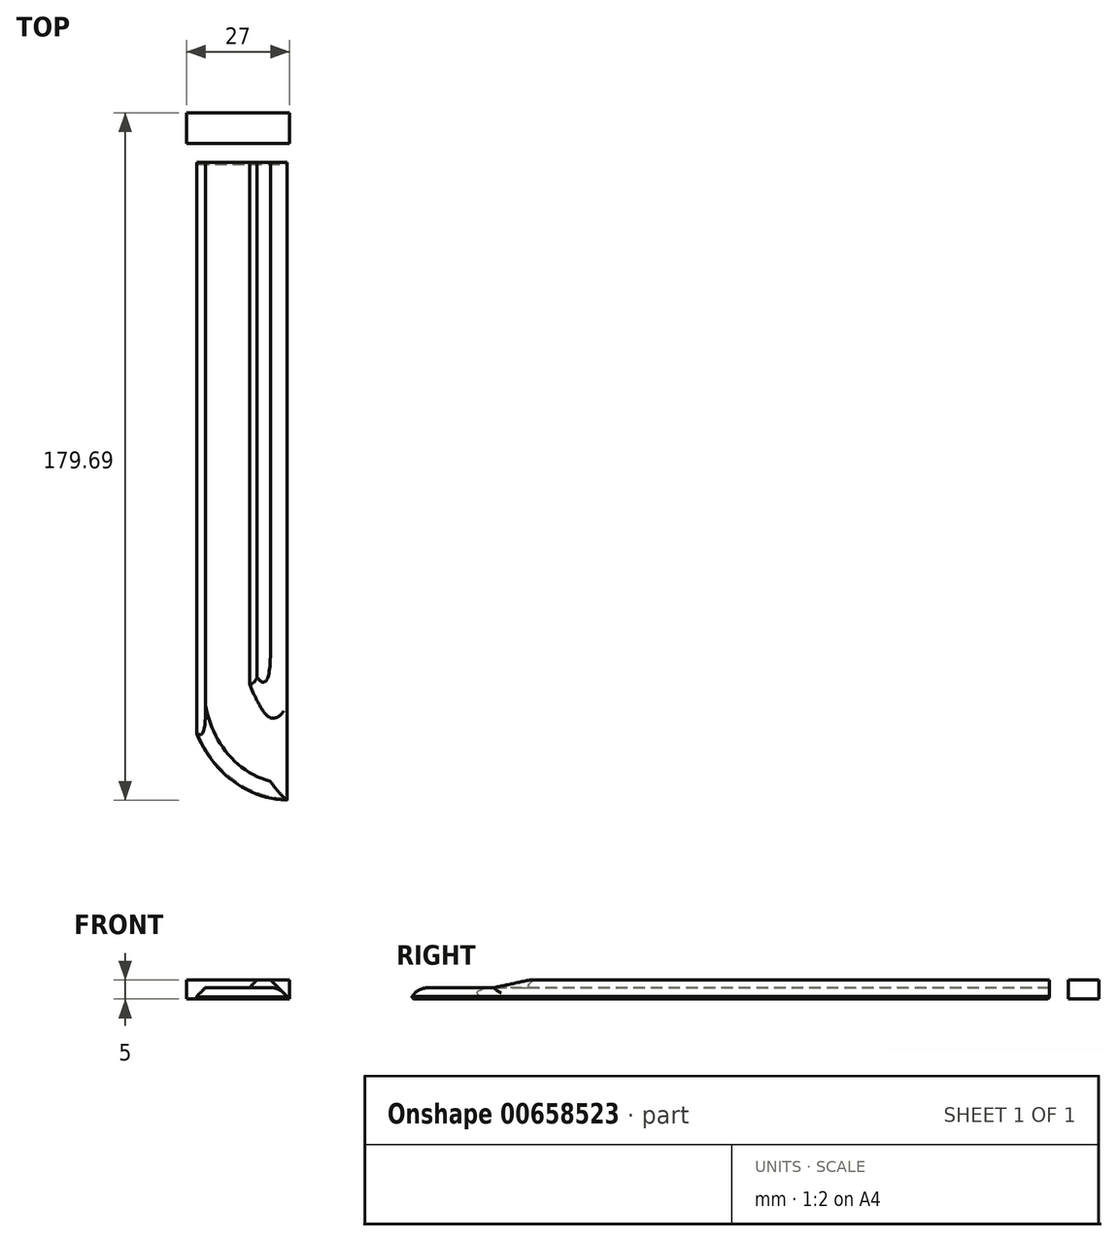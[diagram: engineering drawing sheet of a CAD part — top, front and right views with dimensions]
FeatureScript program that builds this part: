
annotation { "Feature Type Name" : "Feature", "Feature Type Description" : "" }
export const myFeature = defineFeature(function(context is Context, id is Id, definition is map)
    precondition{}
    {
        {
            var Q0;
            Q0=qCreatedBy(makeId("Top.planeOp"),FACE);
            var sketch = newSketch(context, id + "F0", { "sketchPlane" : qUnion([Q0])});
            skLineSegment(sketch, "E0.bottom", {"start": v(-13.5, 4) * mm, "end": v(13.5, 4) * mm});
            skLineSegment(sketch, "E0.top", {"start": v(-13.5, -4) * mm, "end": v(13.5, -4) * mm});
            skLineSegment(sketch, "E0.left", {"start": v(-13.5, 4) * mm, "end": v(-13.5, -4) * mm});
            skLineSegment(sketch, "E0.right", {"start": v(13.5, 4) * mm, "end": v(13.5, -4) * mm});
            skPoint(sketch, "E0.middle", {"position": v(0, 0) * mm});
            skLineSegment(sketch, "E1.bottom", {"start": v(13.5, -4) * mm, "end": v(0, -4) * mm});
            skLineSegment(sketch, "E1.top", {"start": v(13.5, -9) * mm, "end": v(0, -9) * mm});
            skLineSegment(sketch, "E1.left", {"start": v(13.5, -4) * mm, "end": v(13.5, -9) * mm});
            skLineSegment(sketch, "E1.right", {"start": v(0, -4) * mm, "end": v(0, -9) * mm});
            skLineSegment(sketch, "E2.bottom", {"start": v(13.5, -9) * mm, "end": v(-13.5, -9) * mm});
            skLineSegment(sketch, "E2.top", {"start": v(13.5, -146) * mm, "end": v(-13.5, -146) * mm});
            skLineSegment(sketch, "E2.left", {"start": v(13.5, -9) * mm, "end": v(13.5, -146) * mm});
            skLineSegment(sketch, "E2.right", {"start": v(-13.5, -9) * mm, "end": v(-13.5, -146) * mm});
            skLineSegment(sketch, "E3", {"start": v(13.5, -146) * mm, "end": v(13.5, -176) * mm});
            skEllipse(sketch, "E4", {"center": v(13.5, -146) * mm, "majorRadius": 30 * mm, "minorRadius": 27 * mm, "majorAxis": v(0, -1)});
            skLineSegment(sketch, "E5", {"start": v(0, -9) * mm, "end": v(0, -146) * mm});
            skLineSegment(sketch, "E6", {"start": v(0, -146) * mm, "end": v(13.5, -176) * mm});
            skSolve(sketch);
        }
        {
            var Q0;
            Q0=makeQuery(id+"F0.imprint","IMPRINT",FACE,{"disambiguationData":[TD([[makeQuery(id+"F0.imprint","IMPRINT",EDGE,{"derivedFrom":sQuery(id+"F0.wireOp",EDGE,"E0.bottom")}),-1.0]])]});
            var Q1;
            {var subQ0=sQuery(id+"F0.wireOp",EDGE,"E2.left");var subQ5=sQuery(id+"F0.wireOp",EDGE,"E4");var subQ6=makeQuery(id+"F0.imprint","INTERSECT",VERTEX,{"derivedFrom":[subQ0,subQ5]});Q1=makeQuery(id+"F0.imprint","IMPRINT",FACE,{"disambiguationData":[TD([[makeQuery(id+"F0.imprint","IMPRINT",EDGE,{"disambiguationData":[TD([[subQ6,-1.0]])],"derivedFrom":subQ5}),-1.0]])]});}
            var Q2;
            {var subQ0=sQuery(id+"F0.wireOp",EDGE,"E2.left");var subQ5=sQuery(id+"F0.wireOp",EDGE,"E4");var subQ6=makeQuery(id+"F0.imprint","INTERSECT",VERTEX,{"derivedFrom":[subQ0,subQ5]});Q2=makeQuery(id+"F0.imprint","IMPRINT",FACE,{"disambiguationData":[TD([[makeQuery(id+"F0.imprint","IMPRINT",EDGE,{"disambiguationData":[TD([[subQ6,-1.0]])],"derivedFrom":subQ5}),1.0]])]});}
            var Q3;
            {var subQ0=sQuery(id+"F0.wireOp",EDGE,"E3");Q3=makeQuery(id+"F0.imprint","IMPRINT",FACE,{"disambiguationData":[TD([[makeQuery(id+"F0.imprint","IMPRINT",EDGE,{"derivedFrom":subQ0}),-1.0]])]});}
            var Q4;
            Q4=makeQuery(id+"F0.imprint","IMPRINT",FACE,{"disambiguationData":[TD([[makeQuery(id+"F0.imprint","IMPRINT",EDGE,{"derivedFrom":sQuery(id+"F0.wireOp",EDGE,"E1.bottom")}),1.0]])]});
            extrude(context, id + "F1", {"entities" : qUnion([Q0, Q1, Q2, Q3, Q4]), "depth" : 5 * mm, "offsetDistance" : 25 * mm});
        }
        {
            var Q0;
            {var subQ3=sQuery(id+"F0.wireOp",EDGE,"E2.right");Q0=makeQuery(id+"F0.imprint","IMPRINT",FACE,{"disambiguationData":[TD([[makeQuery(id+"F0.imprint","IMPRINT",EDGE,{"derivedFrom":subQ3}),1.0]])]});}
            var Q1;
            {var subQ3=sQuery(id+"F0.wireOp",EDGE,"E6");Q1=makeQuery(id+"F0.imprint","IMPRINT",FACE,{"disambiguationData":[TD([[makeQuery(id+"F0.imprint","IMPRINT",EDGE,{"derivedFrom":subQ3}),-1.0]])]});}
            var Q2;
            {var subQ0=sQuery(id+"F0.wireOp",EDGE,"E4");var subQ3=sQuery(id+"F0.wireOp",EDGE,"E5");var subQ5=makeQuery(id+"F0.imprint","INTERSECT",VERTEX,{"derivedFrom":[subQ0,subQ3]});Q2=makeQuery(id+"F0.imprint","IMPRINT",FACE,{"disambiguationData":[TD([[makeQuery(id+"F0.imprint","IMPRINT",EDGE,{"disambiguationData":[TD([[subQ5,-1.0]])],"derivedFrom":subQ0}),1.0]])]});}
            extrude(context, id + "F2", {"entities" : qUnion([Q0, Q1, Q2]), "operationType" : NewBodyOperationType.ADD, "depth" : 3 * mm, "offsetDistance" : 25 * mm});
        }
        {
            var Q0;
            Q0=makeQuery(id+"F2.opExtrude","CAP_EDGE",EDGE,{"disambiguationData":[OSD([sQuery(id+"F0.wireOp",EDGE,"E2.right")])],"isStart":false});
            var Q1;
            Q1=makeQuery(id+"F1.opExtrude","CAP_EDGE",EDGE,{"disambiguationData":[OSD([sQuery(id+"F0.wireOp",EDGE,"E1.right"),sQuery(id+"F0.wireOp",EDGE,"E5")])],"isStart":false});
            var Q2;
            Q2=makeQuery(id+"F1.opExtrude","CAP_EDGE",EDGE,{"disambiguationData":[OSD([sQuery(id+"F0.wireOp",EDGE,"E6")])],"isStart":false});
            var Q3;
            Q3=makeQuery(id+"F1.opExtrude","CAP_EDGE",EDGE,{"disambiguationData":[OSD([sQuery(id+"F0.wireOp",EDGE,"E0.right"),sQuery(id+"F0.wireOp",EDGE,"E1.left"),sQuery(id+"F0.wireOp",EDGE,"E2.left"),sQuery(id+"F0.wireOp",EDGE,"E3")])],"isStart":false});
            chamfer(context, id + "F3", {"entities" : qUnion([Q0, Q1, Q2, Q3]), "width" : 5 * mm});
        }
        {
            var Q0;
            Q0=makeQuery(id+"F2.opExtrude","CAP_EDGE",EDGE,{"disambiguationData":[OSD([sQuery(id+"F0.wireOp",EDGE,"E4")])],"isStart":false});
            var Q1;
            {var subQ0=sQuery(id+"F0.wireOp",EDGE,"E3");var subQ1=sQuery(id+"F0.wireOp",EDGE,"E2.left");var subQ2=sQuery(id+"F0.wireOp",EDGE,"E1.left");var subQ3=sQuery(id+"F0.wireOp",EDGE,"E0.right");Q1=makeQuery(id+"F3.opChamfer","BLEND_EDGE",EDGE,{"blendedFrom":[makeQuery(id+"F1.opExtrude","CAP_EDGE",EDGE,{"disambiguationData":[OSD([subQ3,subQ2,subQ1,subQ0])],"isStart":false}),makeQuery(id+"F1.opExtrude","CAP_FACE",FACE,{"disambiguationData":[OSD([sQuery(id+"F0.wireOp",EDGE,"E0.bottom"),sQuery(id+"F0.wireOp",EDGE,"E0.top"),sQuery(id+"F0.wireOp",EDGE,"E0.left"),subQ3,subQ2,sQuery(id+"F0.wireOp",EDGE,"E1.right"),subQ1,subQ0,sQuery(id+"F0.wireOp",EDGE,"E5"),sQuery(id+"F0.wireOp",EDGE,"E6")])],"isStart":false})],"blendedInto":[makeQuery(id+"F1.opExtrude","CAP_FACE",FACE,{"disambiguationData":[OSD([sQuery(id+"F0.wireOp",EDGE,"E0.bottom"),sQuery(id+"F0.wireOp",EDGE,"E0.top"),sQuery(id+"F0.wireOp",EDGE,"E0.left"),subQ3,subQ2,sQuery(id+"F0.wireOp",EDGE,"E1.right"),subQ1,subQ0,sQuery(id+"F0.wireOp",EDGE,"E5"),sQuery(id+"F0.wireOp",EDGE,"E6")])],"isStart":false})]});}
            var Q2;
            Q2=makeQuery(id+"F3.opChamfer","BLEND_EDGE",EDGE,{"blendedFrom":[makeQuery(id+"F1.opExtrude","CAP_EDGE",EDGE,{"disambiguationData":[OSD([sQuery(id+"F0.wireOp",EDGE,"E0.right"),sQuery(id+"F0.wireOp",EDGE,"E1.left"),sQuery(id+"F0.wireOp",EDGE,"E2.left"),sQuery(id+"F0.wireOp",EDGE,"E3")])],"isStart":false}),makeQuery(id+"F2.opExtrude","CAP_FACE",FACE,{"disambiguationData":[OSD([sQuery(id+"F0.wireOp",EDGE,"E2.bottom"),sQuery(id+"F0.wireOp",EDGE,"E2.right"),sQuery(id+"F0.wireOp",EDGE,"E4"),sQuery(id+"F0.wireOp",EDGE,"E5"),sQuery(id+"F0.wireOp",EDGE,"E6")])],"isStart":false})],"blendedInto":[makeQuery(id+"F2.opExtrude","CAP_FACE",FACE,{"disambiguationData":[OSD([sQuery(id+"F0.wireOp",EDGE,"E2.bottom"),sQuery(id+"F0.wireOp",EDGE,"E2.right"),sQuery(id+"F0.wireOp",EDGE,"E4"),sQuery(id+"F0.wireOp",EDGE,"E5"),sQuery(id+"F0.wireOp",EDGE,"E6")])],"isStart":false})]});
            var Q3;
            Q3=makeQuery(id+"F3.opChamfer","BLEND_EDGE",EDGE,{"blendedFrom":[makeQuery(id+"F1.opExtrude","CAP_EDGE",EDGE,{"disambiguationData":[OSD([sQuery(id+"F0.wireOp",EDGE,"E0.right"),sQuery(id+"F0.wireOp",EDGE,"E1.left"),sQuery(id+"F0.wireOp",EDGE,"E2.left"),sQuery(id+"F0.wireOp",EDGE,"E3")])],"isStart":false}),makeQuery(id+"F1.opExtrude","CAP_EDGE",EDGE,{"disambiguationData":[OSD([sQuery(id+"F0.wireOp",EDGE,"E6")])],"isStart":false})],"blendedInto":[]});
            fillet(context, id + "F4", {"entities" : qUnion([Q0, Q1, Q2, Q3]), "radius" : 5 * mm, "rho" : 0.5, "crossSection" : FilletCrossSection.CONIC, "allowEdgeOverflow" : false});
        }
        {
            var Q0;
            {var subQ0=sQuery(id+"F0.wireOp",EDGE,"E6");var subQ1=sQuery(id+"F0.wireOp",EDGE,"E5");Q0=makeQuery(id+"F2.boolean.opBoolean","MERGE",FACE,{"derivedFrom":[makeQuery(id+"F1.opExtrude","CAP_FACE",FACE,{"disambiguationData":[OSD([sQuery(id+"F0.wireOp",EDGE,"E0.bottom"),sQuery(id+"F0.wireOp",EDGE,"E0.top"),sQuery(id+"F0.wireOp",EDGE,"E0.left"),sQuery(id+"F0.wireOp",EDGE,"E0.right"),sQuery(id+"F0.wireOp",EDGE,"E1.left"),sQuery(id+"F0.wireOp",EDGE,"E1.right"),sQuery(id+"F0.wireOp",EDGE,"E2.left"),sQuery(id+"F0.wireOp",EDGE,"E3"),subQ1,subQ0])],"isStart":true}),makeQuery(id+"F2.opExtrude","CAP_FACE",FACE,{"disambiguationData":[OSD([sQuery(id+"F0.wireOp",EDGE,"E2.bottom"),sQuery(id+"F0.wireOp",EDGE,"E2.right"),sQuery(id+"F0.wireOp",EDGE,"E4"),subQ1,subQ0])],"isStart":true})]});}
            chamfer(context, id + "F5", {"entities" : qUnion([Q0]), "width" : 0.4 * mm, "tangentPropagation" : true});
        }
    });
